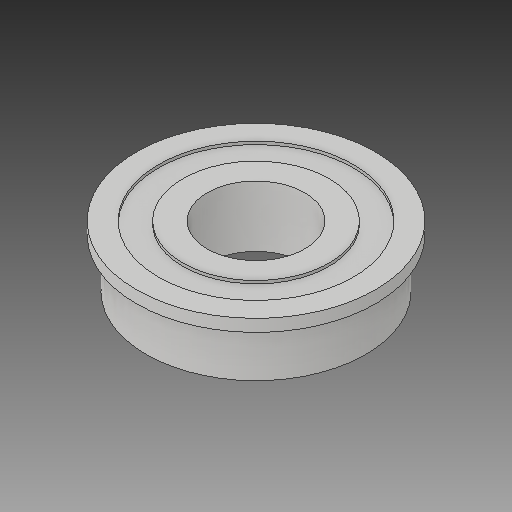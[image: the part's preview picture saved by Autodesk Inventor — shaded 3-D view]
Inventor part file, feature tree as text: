
AUTODESK INVENTOR PART (.ipt)
format: ipt  version: 2018 (Build 220112000, 112)  size: 126,464 bytes
history: native  units: in
note: dims shown in document units (in); Inventor stores cm internally (conversion verified against a paired STEP export)
features: revolve x1
ambient origin geometry x8: Origin, YZ Plane, XZ Plane, XY Plane, X Axis, Y Axis, Z Axis, Center Point
bodies: Solid1 (feature_tree)
feature tree (1):
  revolve  "Revolve1"  [1 undecoded]
note: 1 required parameter value undecoded (feature->parameter linkage not recoverable at this tier; creation-order binding heuristic only, values carry confidence <= 0.55)
